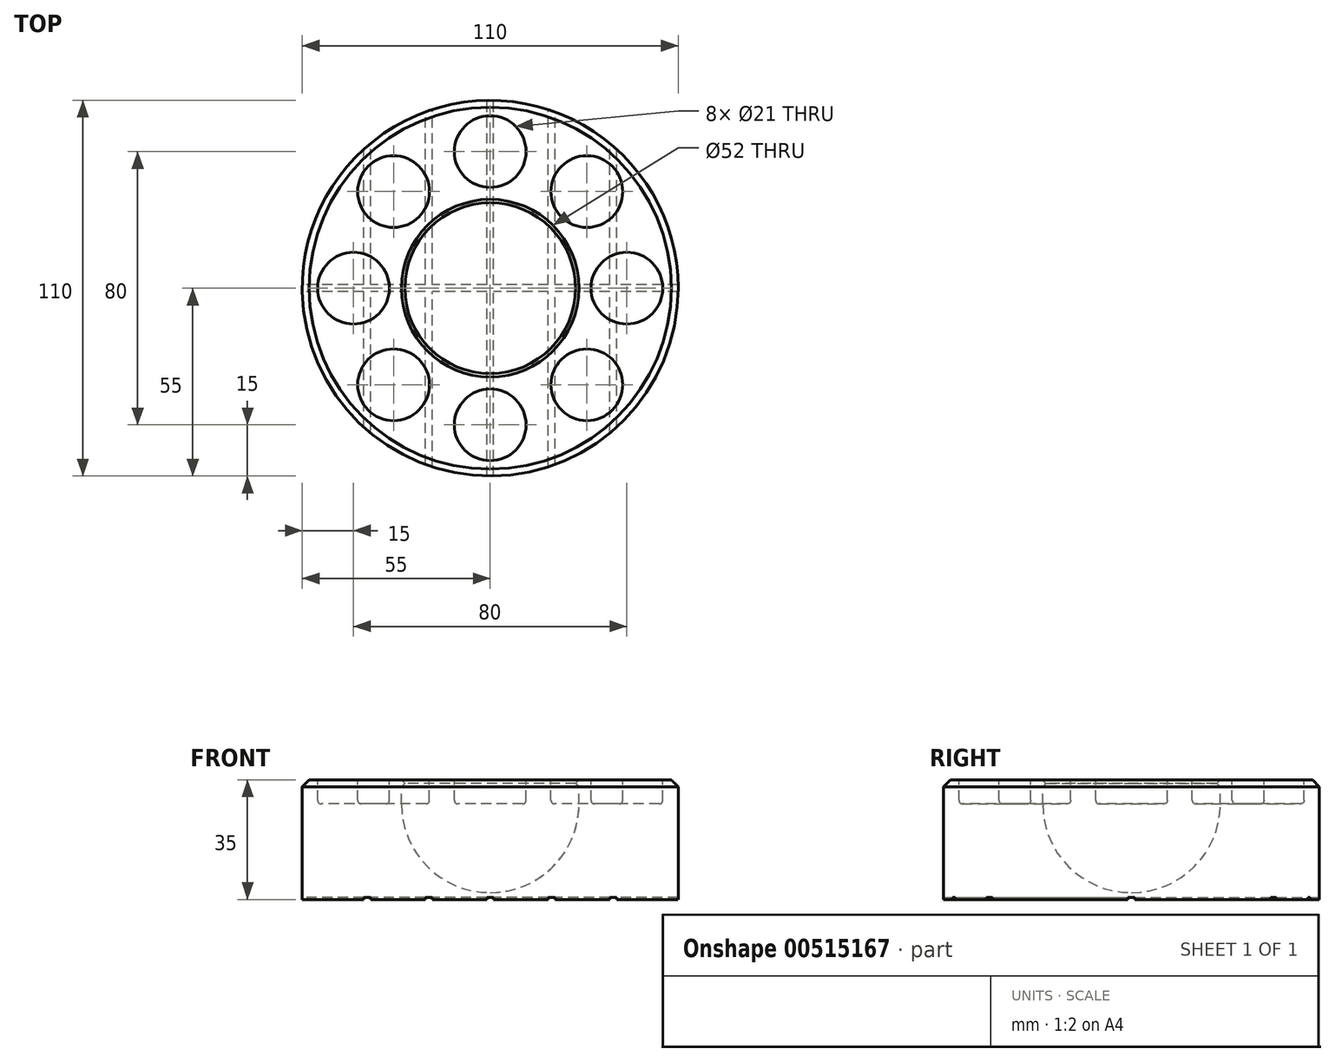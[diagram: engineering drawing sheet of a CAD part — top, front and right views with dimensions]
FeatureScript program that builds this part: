
annotation { "Feature Type Name" : "Feature", "Feature Type Description" : "" }
export const myFeature = defineFeature(function(context is Context, id is Id, definition is map)
    precondition{}
    {
        {
            var Q0;
            Q0=qCreatedBy(makeId("Top.planeOp"),FACE);
            var sketch = newSketch(context, id + "F0", { "sketchPlane" : qUnion([Q0])});
            skLineSegment(sketch, "E0.bottom", {"start": v(0, 0) * mm, "end": v(110, 0) * mm});
            skLineSegment(sketch, "E0.top", {"start": v(0, -110) * mm, "end": v(110, -110) * mm});
            skLineSegment(sketch, "E0.left", {"start": v(0, 0) * mm, "end": v(0, -110) * mm});
            skLineSegment(sketch, "E0.right", {"start": v(110, 0) * mm, "end": v(110, -110) * mm});
            skSolve(sketch);
        }
        {
            var Q0;
            Q0=qSketchRegion(id+"F0",true);
            extrude(context, id + "F1", {"entities" : qUnion([Q0]), "depth" : 35 * mm, "offsetDistance" : 25 * mm});
        }
        {
            var Q0;
            Q0=makeQuery(id+"F1.opExtrude","CAP_FACE",FACE,{"disambiguationData":[OSD([sQuery(id+"F0.wireOp",EDGE,"E0.bottom"),sQuery(id+"F0.wireOp",EDGE,"E0.top"),sQuery(id+"F0.wireOp",EDGE,"E0.left"),sQuery(id+"F0.wireOp",EDGE,"E0.right")])],"isStart":false});
            var sketch = newSketch(context, id + "F2", { "sketchPlane" : qUnion([Q0])});
            skCircle(sketch, "E1", {"center": v(55, -55) * mm, "radius": 26 * mm});
            skSolve(sketch);
        }
        {
            var Q0;
            Q0=qSketchRegion(id+"F2",true);
            extrude(context, id + "F3", {"entities" : qUnion([Q0]), "operationType" : NewBodyOperationType.REMOVE, "oppositeDirection" : true, "depth" : 33 * mm, "offsetDistance" : 25 * mm});
        }
        {
            var Q0;
            Q0=makeQuery(id+"F3.boolean.opBoolean","COPY",EDGE,{"derivedFrom":makeQuery(id+"F3.opExtrude","CAP_EDGE",EDGE,{"disambiguationData":[OSD([sQuery(id+"F2.wireOp",EDGE,"E1")])],"isStart":false})});
            fillet(context, id + "F4", {"entities" : qUnion([Q0]), "radius" : 26 * mm, "tangentPropagation" : true, "allowEdgeOverflow" : false});
        }
        {
            var Q0;
            Q0=makeQuery(id+"F1.opExtrude","CAP_FACE",FACE,{"disambiguationData":[OSD([sQuery(id+"F0.wireOp",EDGE,"E0.bottom"),sQuery(id+"F0.wireOp",EDGE,"E0.top"),sQuery(id+"F0.wireOp",EDGE,"E0.left"),sQuery(id+"F0.wireOp",EDGE,"E0.right")])],"isStart":false});
            var sketch = newSketch(context, id + "F5", { "sketchPlane" : qUnion([Q0])});
            skCircle(sketch, "E2", {"center": v(55, -55) * mm, "radius": 26 * mm});
            skCircle(sketch, "E3", {"center": v(55, -55) * mm, "radius": 25 * mm});
            skSolve(sketch);
        }
        {
            var Q0;
            Q0=qSketchRegion(id+"F5",true);
            extrude(context, id + "F6", {"entities" : qUnion([Q0]), "operationType" : NewBodyOperationType.ADD, "oppositeDirection" : true, "depth" : 2 * mm, "offsetDistance" : 25 * mm});
        }
        {
            var Q0;
            Q0=makeQuery(id+"F6.opExtrude","CAP_EDGE",EDGE,{"disambiguationData":[OSD([sQuery(id+"F5.wireOp",EDGE,"E3")])],"isStart":true});
            chamfer(context, id + "F7", {"entities" : qUnion([Q0]), "width" : 1 * mm, "tangentPropagation" : true});
        }
        {
            var Q0;
            Q0=makeQuery(id+"F6.opExtrude","CAP_EDGE",EDGE,{"disambiguationData":[OSD([sQuery(id+"F5.wireOp",EDGE,"E3")])],"isStart":false});
            chamfer(context, id + "F8", {"entities" : qUnion([Q0]), "width" : 1 * mm, "tangentPropagation" : true});
        }
        {
            var Q0;
            Q0=makeQuery(id+"F6.boolean.opBoolean","MERGE",FACE,{"derivedFrom":[makeQuery(id+"F1.opExtrude","CAP_FACE",FACE,{"disambiguationData":[OSD([sQuery(id+"F0.wireOp",EDGE,"E0.bottom"),sQuery(id+"F0.wireOp",EDGE,"E0.top"),sQuery(id+"F0.wireOp",EDGE,"E0.left"),sQuery(id+"F0.wireOp",EDGE,"E0.right")])],"isStart":false}),makeQuery(id+"F6.opExtrude","CAP_FACE",FACE,{"disambiguationData":[OSD([sQuery(id+"F5.wireOp",EDGE,"E2"),sQuery(id+"F5.wireOp",EDGE,"E3")])],"isStart":true})]});
            var sketch = newSketch(context, id + "F9", { "sketchPlane" : qUnion([Q0])});
            skCircle(sketch, "E4", {"center": v(83.28, -26.72) * mm, "radius": 10.5 * mm});
            skCircle(sketch, "E5", {"center": v(26.72, -26.72) * mm, "radius": 10.5 * mm});
            skCircle(sketch, "E6", {"center": v(26.72, -83.28) * mm, "radius": 10.5 * mm});
            skCircle(sketch, "E7", {"center": v(83.28, -83.28) * mm, "radius": 10.5 * mm});
            skCircle(sketch, "E8", {"center": v(55, -15) * mm, "radius": 10.5 * mm});
            skCircle(sketch, "E9", {"center": v(95, -55) * mm, "radius": 10.5 * mm});
            skCircle(sketch, "E10", {"center": v(55, -95) * mm, "radius": 10.5 * mm});
            skPoint(sketch, "E10.centerSnap0", {"position": v(55, -110) * mm});
            skCircle(sketch, "E11", {"center": v(15, -55) * mm, "radius": 10.5 * mm});
            skSolve(sketch);
        }
        {
            var Q0;
            Q0=qSketchRegion(id+"F9",true);
            extrude(context, id + "F10", {"entities" : qUnion([Q0]), "operationType" : NewBodyOperationType.REMOVE, "oppositeDirection" : true, "depth" : 7 * mm, "offsetDistance" : 25 * mm});
        }
        {
            var Q0;
            Q0=makeQuery(id+"F10.boolean.opBoolean","COPY",EDGE,{"derivedFrom":makeQuery(id+"F10.opExtrude","CAP_EDGE",EDGE,{"disambiguationData":[OSD([sQuery(id+"F9.wireOp",EDGE,"E5")])],"isStart":false})});
            var Q1;
            Q1=makeQuery(id+"F10.boolean.opBoolean","COPY",EDGE,{"derivedFrom":makeQuery(id+"F10.opExtrude","CAP_EDGE",EDGE,{"disambiguationData":[OSD([sQuery(id+"F9.wireOp",EDGE,"E8")])],"isStart":false})});
            var Q2;
            Q2=makeQuery(id+"F10.boolean.opBoolean","COPY",EDGE,{"derivedFrom":makeQuery(id+"F10.opExtrude","CAP_EDGE",EDGE,{"disambiguationData":[OSD([sQuery(id+"F9.wireOp",EDGE,"E4")])],"isStart":false})});
            var Q3;
            Q3=makeQuery(id+"F10.boolean.opBoolean","COPY",EDGE,{"derivedFrom":makeQuery(id+"F10.opExtrude","CAP_EDGE",EDGE,{"disambiguationData":[OSD([sQuery(id+"F9.wireOp",EDGE,"E9")])],"isStart":false})});
            var Q4;
            Q4=makeQuery(id+"F10.boolean.opBoolean","COPY",EDGE,{"derivedFrom":makeQuery(id+"F10.opExtrude","CAP_EDGE",EDGE,{"disambiguationData":[OSD([sQuery(id+"F9.wireOp",EDGE,"E7")])],"isStart":false})});
            var Q5;
            Q5=makeQuery(id+"F10.boolean.opBoolean","COPY",EDGE,{"derivedFrom":makeQuery(id+"F10.opExtrude","CAP_EDGE",EDGE,{"disambiguationData":[OSD([sQuery(id+"F9.wireOp",EDGE,"E10")])],"isStart":false})});
            var Q6;
            Q6=makeQuery(id+"F10.boolean.opBoolean","COPY",EDGE,{"derivedFrom":makeQuery(id+"F10.opExtrude","CAP_EDGE",EDGE,{"disambiguationData":[OSD([sQuery(id+"F9.wireOp",EDGE,"E6")])],"isStart":false})});
            var Q7;
            Q7=makeQuery(id+"F10.boolean.opBoolean","COPY",EDGE,{"derivedFrom":makeQuery(id+"F10.opExtrude","CAP_EDGE",EDGE,{"disambiguationData":[OSD([sQuery(id+"F9.wireOp",EDGE,"E11")])],"isStart":false})});
            fillet(context, id + "F11", {"entities" : qUnion([Q0, Q1, Q2, Q3, Q4, Q5, Q6, Q7]), "radius" : 1 * mm, "tangentPropagation" : true, "allowEdgeOverflow" : false});
        }
        {
            var Q0;
            Q0=makeQuery(id+"F1.opExtrude","SWEPT_EDGE",EDGE,{"disambiguationData":[OSD([sQuery(id+"F0.wireOp",EDGE,"E0.bottom"),sQuery(id+"F0.wireOp",EDGE,"E0.left")])]});
            var Q1;
            Q1=makeQuery(id+"F1.opExtrude","SWEPT_EDGE",EDGE,{"disambiguationData":[OSD([sQuery(id+"F0.wireOp",EDGE,"E0.top"),sQuery(id+"F0.wireOp",EDGE,"E0.left")])]});
            var Q2;
            Q2=makeQuery(id+"F1.opExtrude","SWEPT_EDGE",EDGE,{"disambiguationData":[OSD([sQuery(id+"F0.wireOp",EDGE,"E0.top"),sQuery(id+"F0.wireOp",EDGE,"E0.right")])]});
            var Q3;
            Q3=makeQuery(id+"F1.opExtrude","SWEPT_EDGE",EDGE,{"disambiguationData":[OSD([sQuery(id+"F0.wireOp",EDGE,"E0.bottom"),sQuery(id+"F0.wireOp",EDGE,"E0.right")])]});
            fillet(context, id + "F12", {"entities" : qUnion([Q0, Q1, Q2, Q3]), "radius" : 55 * mm, "tangentPropagation" : true, "allowEdgeOverflow" : false});
        }
        {
            var Q0;
            {var subQ0=sQuery(id+"F0.wireOp",EDGE,"E0.left");var subQ1=sQuery(id+"F0.wireOp",EDGE,"E0.bottom");Q0=makeQuery(id+"F12.opFillet","BLEND_EDGE",EDGE,{"blendedFrom":[makeQuery(id+"F1.opExtrude","SWEPT_EDGE",EDGE,{"disambiguationData":[OSD([subQ1,subQ0])]}),makeQuery(id+"F6.boolean.opBoolean","MERGE",FACE,{"derivedFrom":[makeQuery(id+"F1.opExtrude","CAP_FACE",FACE,{"disambiguationData":[OSD([subQ1,sQuery(id+"F0.wireOp",EDGE,"E0.top"),subQ0,sQuery(id+"F0.wireOp",EDGE,"E0.right")])],"isStart":false}),makeQuery(id+"F6.opExtrude","CAP_FACE",FACE,{"disambiguationData":[OSD([sQuery(id+"F5.wireOp",EDGE,"E2"),sQuery(id+"F5.wireOp",EDGE,"E3")])],"isStart":true})]})],"blendedInto":[makeQuery(id+"F6.boolean.opBoolean","MERGE",FACE,{"derivedFrom":[makeQuery(id+"F1.opExtrude","CAP_FACE",FACE,{"disambiguationData":[OSD([subQ1,sQuery(id+"F0.wireOp",EDGE,"E0.top"),subQ0,sQuery(id+"F0.wireOp",EDGE,"E0.right")])],"isStart":false}),makeQuery(id+"F6.opExtrude","CAP_FACE",FACE,{"disambiguationData":[OSD([sQuery(id+"F5.wireOp",EDGE,"E2"),sQuery(id+"F5.wireOp",EDGE,"E3")])],"isStart":true})]})]});}
            chamfer(context, id + "F13", {"entities" : qUnion([Q0]), "width" : 2 * mm, "tangentPropagation" : true});
        }
        {
            var Q0;
            Q0=makeQuery(id+"F1.opExtrude","CAP_FACE",FACE,{"disambiguationData":[OSD([sQuery(id+"F0.wireOp",EDGE,"E0.bottom"),sQuery(id+"F0.wireOp",EDGE,"E0.top"),sQuery(id+"F0.wireOp",EDGE,"E0.left"),sQuery(id+"F0.wireOp",EDGE,"E0.right")])],"isStart":true});
            var sketch = newSketch(context, id + "F14", { "sketchPlane" : qUnion([Q0])});
            skLineSegment(sketch, "E12.bottom", {"start": v(110, 56) * mm, "end": v(92, 56) * mm});
            skLineSegment(sketch, "E12.top", {"start": v(110, 54) * mm, "end": v(92, 54) * mm});
            skLineSegment(sketch, "E12.left", {"start": v(110, 56) * mm, "end": v(110, 54) * mm});
            skLineSegment(sketch, "E12.right", {"start": v(0, 56) * mm, "end": v(0, 54) * mm});
            skLineSegment(sketch, "E13.bottom", {"start": v(56, 110) * mm, "end": v(54, 110) * mm});
            skLineSegment(sketch, "E13.top", {"start": v(56, 0) * mm, "end": v(54, 0) * mm});
            skLineSegment(sketch, "E13.left", {"start": v(56, 110) * mm, "end": v(56, 56) * mm});
            skLineSegment(sketch, "E13.right", {"start": v(54, 110) * mm, "end": v(54, 56) * mm});
            skLineSegment(sketch, "E14.trimOffspring", {"start": v(54, 56) * mm, "end": v(38, 56) * mm});
            skLineSegment(sketch, "E15.trimOffspring", {"start": v(56, 54) * mm, "end": v(56, 0) * mm});
            skLineSegment(sketch, "E16.trimOffspring", {"start": v(54, 54) * mm, "end": v(38, 54) * mm});
            skLineSegment(sketch, "E17.trimOffspring", {"start": v(54, 54) * mm, "end": v(54, 0) * mm});
            skPoint(sketch, "E18.oppositeSnap0", {"position": v(83, 56) * mm});
            skLineSegment(sketch, "E19.bottom", {"start": v(38, 113.96) * mm, "end": v(36, 113.96) * mm});
            skLineSegment(sketch, "E19.top", {"start": v(38, -14.38) * mm, "end": v(36, -14.38) * mm});
            skLineSegment(sketch, "E19.left", {"start": v(38, 113.96) * mm, "end": v(38, 56) * mm});
            skLineSegment(sketch, "E19.right", {"start": v(36, 113.96) * mm, "end": v(36, 56) * mm});
            skLineSegment(sketch, "E20.bottom", {"start": v(92, 102.54) * mm, "end": v(90, 102.54) * mm});
            skLineSegment(sketch, "E20.top", {"start": v(92, 8.46) * mm, "end": v(90, 8.46) * mm});
            skLineSegment(sketch, "E20.left", {"start": v(92, 102.54) * mm, "end": v(92, 56) * mm});
            skLineSegment(sketch, "E20.right", {"start": v(90, 102.54) * mm, "end": v(90, 56) * mm});
            skLineSegment(sketch, "E21.bottom", {"start": v(20, 111.37) * mm, "end": v(18, 111.37) * mm});
            skLineSegment(sketch, "E21.top", {"start": v(20, -4.7) * mm, "end": v(18, -4.7) * mm});
            skLineSegment(sketch, "E21.left", {"start": v(20, 111.37) * mm, "end": v(20, 56) * mm});
            skLineSegment(sketch, "E21.right", {"start": v(18, 111.37) * mm, "end": v(18, 56) * mm});
            skLineSegment(sketch, "E22.bottom", {"start": v(74, 112.14) * mm, "end": v(72, 112.14) * mm});
            skLineSegment(sketch, "E22.top", {"start": v(74, -1.19) * mm, "end": v(72, -1.19) * mm});
            skLineSegment(sketch, "E22.left", {"start": v(74, 112.14) * mm, "end": v(74, 56) * mm});
            skLineSegment(sketch, "E22.right", {"start": v(72, 112.14) * mm, "end": v(72, 56) * mm});
            skLineSegment(sketch, "E23.trimOffspring", {"start": v(92, 54) * mm, "end": v(92, 8.46) * mm});
            skLineSegment(sketch, "E24.trimOffspring", {"start": v(90, 56) * mm, "end": v(74, 56) * mm});
            skLineSegment(sketch, "E25.trimOffspring", {"start": v(90, 54) * mm, "end": v(74, 54) * mm});
            skLineSegment(sketch, "E26.trimOffspring", {"start": v(90, 54) * mm, "end": v(90, 8.46) * mm});
            skLineSegment(sketch, "E27.trimOffspring", {"start": v(74, 54) * mm, "end": v(74, -1.19) * mm});
            skLineSegment(sketch, "E28.trimOffspring", {"start": v(72, 54) * mm, "end": v(72, -1.19) * mm});
            skLineSegment(sketch, "E29.trimOffspring", {"start": v(72, 56) * mm, "end": v(56, 56) * mm});
            skLineSegment(sketch, "E30.trimOffspring", {"start": v(72, 54) * mm, "end": v(56, 54) * mm});
            skLineSegment(sketch, "E31.trimOffspring", {"start": v(38, 54) * mm, "end": v(38, -14.38) * mm});
            skLineSegment(sketch, "E32.trimOffspring", {"start": v(36, 54) * mm, "end": v(36, -14.38) * mm});
            skLineSegment(sketch, "E33.trimOffspring", {"start": v(36, 56) * mm, "end": v(20, 56) * mm});
            skLineSegment(sketch, "E34.trimOffspring", {"start": v(36, 54) * mm, "end": v(20, 54) * mm});
            skLineSegment(sketch, "E35.trimOffspring", {"start": v(18, 56) * mm, "end": v(0, 56) * mm});
            skLineSegment(sketch, "E36.trimOffspring", {"start": v(20, 54) * mm, "end": v(20, -4.7) * mm});
            skLineSegment(sketch, "E37.trimOffspring", {"start": v(18, 54) * mm, "end": v(0, 54) * mm});
            skLineSegment(sketch, "E38.trimOffspring", {"start": v(18, 54) * mm, "end": v(18, -4.7) * mm});
            skSolve(sketch);
        }
        {
            var Q0;
            Q0=qSketchRegion(id+"F14",true);
            extrude(context, id + "F15", {"entities" : qUnion([Q0]), "operationType" : NewBodyOperationType.REMOVE, "oppositeDirection" : true, "depth" : 0.6 * mm, "offsetDistance" : 25 * mm});
        }
    });
